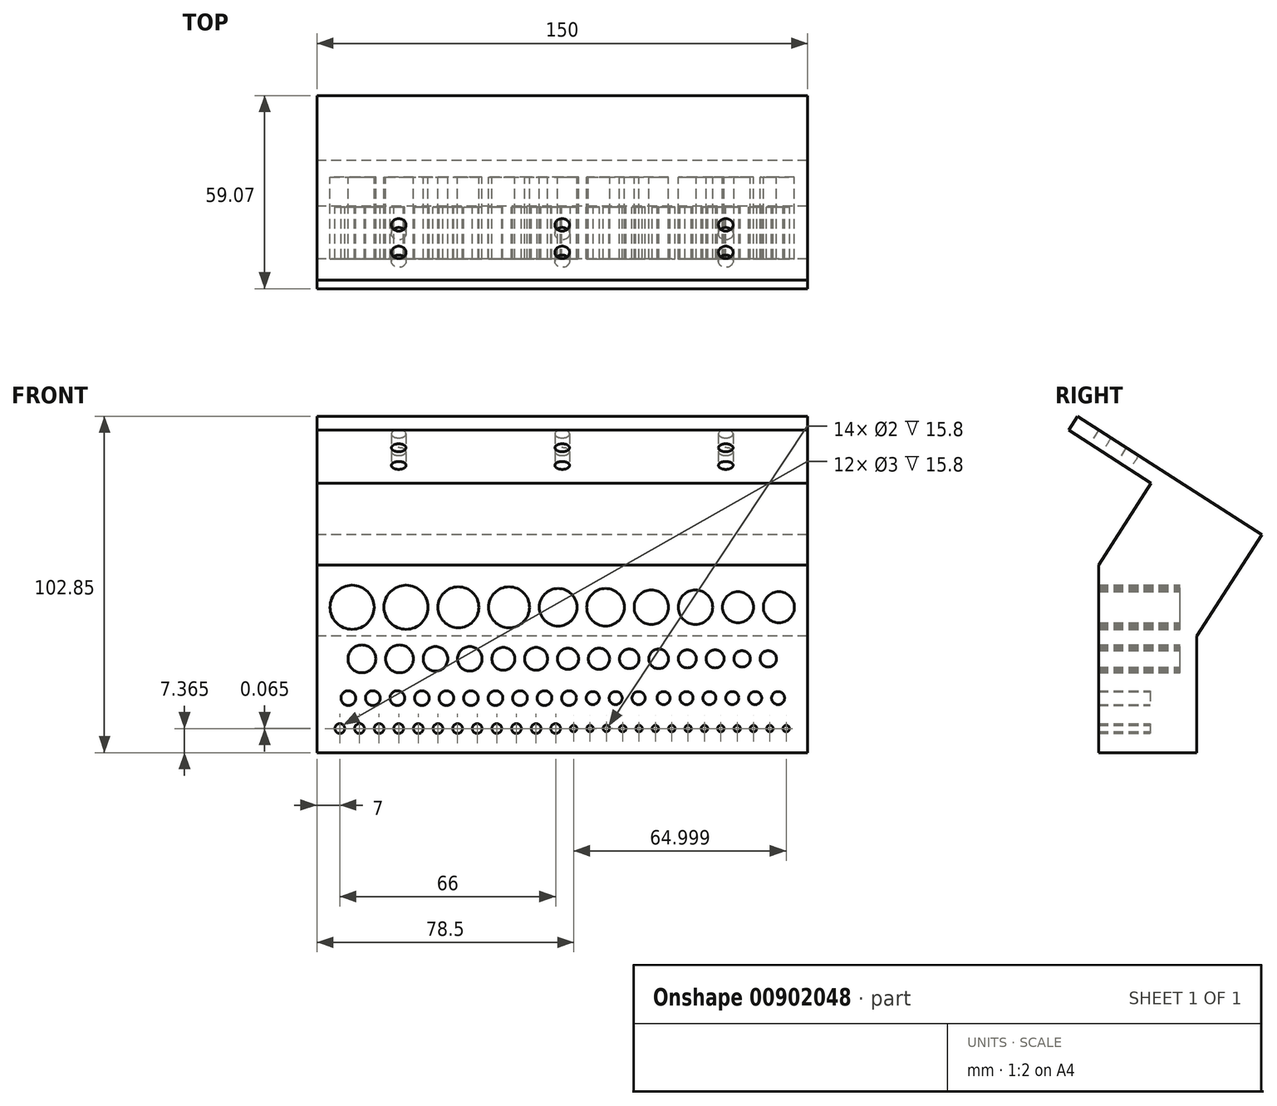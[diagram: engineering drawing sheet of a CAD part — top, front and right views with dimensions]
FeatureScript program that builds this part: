
annotation { "Feature Type Name" : "Feature", "Feature Type Description" : "" }
export const myFeature = defineFeature(function(context is Context, id is Id, definition is map)
    precondition{}
    {
        {
            var Q0;
            Q0=qCreatedBy(makeId("Front.planeOp"),FACE);
            var sketch = newSketch(context, id + "F0", { "sketchPlane" : qUnion([Q0])});
            skLineSegment(sketch, "E0.bottom", {"start": v(75, 28.68) * mm, "end": v(-75, 28.68) * mm});
            skLineSegment(sketch, "E0.top", {"start": v(75, -28.68) * mm, "end": v(-75, -28.68) * mm});
            skLineSegment(sketch, "E0.left", {"start": v(75, 28.68) * mm, "end": v(75, -28.68) * mm});
            skLineSegment(sketch, "E0.right", {"start": v(-75, 28.68) * mm, "end": v(-75, -28.68) * mm});
            skPoint(sketch, "E0.middle", {"position": v(0, 0) * mm});
            skLineSegment(sketch, "E1", {"start": v(-75, 0) * mm, "end": v(75, 0) * mm});
            skLineSegment(sketch, "E2", {"start": v(-75, 15.78) * mm, "end": v(75, 15.78) * mm});
            skLineSegment(sketch, "E3", {"start": v(-75, -12) * mm, "end": v(75, -12) * mm});
            skCircle(sketch, "E4", {"center": v(-64.25, 15.78) * mm, "radius": 6.75 * mm});
            skCircle(sketch, "E5", {"center": v(-47.75, 15.78) * mm, "radius": 6.75 * mm});
            skCircle(sketch, "E6", {"center": v(-31.75, 15.78) * mm, "radius": 6.25 * mm});
            skCircle(sketch, "E7", {"center": v(-16.25, 15.78) * mm, "radius": 6.25 * mm});
            skCircle(sketch, "E8", {"center": v(-1.25, 15.78) * mm, "radius": 5.75 * mm});
            skCircle(sketch, "E9", {"center": v(13.25, 15.78) * mm, "radius": 5.75 * mm});
            skCircle(sketch, "E10", {"center": v(27.25, 15.78) * mm, "radius": 5.25 * mm});
            skCircle(sketch, "E11", {"center": v(40.75, 15.78) * mm, "radius": 5.25 * mm});
            skCircle(sketch, "E12", {"center": v(53.75, 15.78) * mm, "radius": 4.75 * mm});
            skCircle(sketch, "E13", {"center": v(66.25, 15.78) * mm, "radius": 4.75 * mm});
            skCircle(sketch, "E14", {"center": v(-61.25, 0) * mm, "radius": 4.25 * mm});
            skCircle(sketch, "E15", {"center": v(-49.75, 0) * mm, "radius": 4.25 * mm});
            skCircle(sketch, "E16", {"center": v(-38.75, 0) * mm, "radius": 3.75 * mm});
            skCircle(sketch, "E17", {"center": v(-28.25, 0) * mm, "radius": 3.75 * mm});
            skCircle(sketch, "E18", {"center": v(-18, 0) * mm, "radius": 3.5 * mm});
            skCircle(sketch, "E19", {"center": v(-8, 0) * mm, "radius": 3.5 * mm});
            skCircle(sketch, "E20", {"center": v(1.75, 0) * mm, "radius": 3.25 * mm});
            skCircle(sketch, "E21", {"center": v(11.25, 0) * mm, "radius": 3.25 * mm});
            skCircle(sketch, "E22", {"center": v(20.5, 0) * mm, "radius": 3 * mm});
            skCircle(sketch, "E23", {"center": v(29.5, 0) * mm, "radius": 3 * mm});
            skCircle(sketch, "E24", {"center": v(38.25, 0) * mm, "radius": 2.75 * mm});
            skCircle(sketch, "E25", {"center": v(46.75, 0) * mm, "radius": 2.75 * mm});
            skCircle(sketch, "E26", {"center": v(55, 0) * mm, "radius": 2.5 * mm});
            skCircle(sketch, "E27", {"center": v(63, 0) * mm, "radius": 2.5 * mm});
            skCircle(sketch, "E28", {"center": v(-65.41, -12) * mm, "radius": 2.25 * mm});
            skCircle(sketch, "E29", {"center": v(-57.91, -12) * mm, "radius": 2.25 * mm});
            skCircle(sketch, "E30", {"center": v(-50.41, -12) * mm, "radius": 2.25 * mm});
            skCircle(sketch, "E31", {"center": v(-42.91, -12) * mm, "radius": 2.25 * mm});
            skCircle(sketch, "E32", {"center": v(-35.41, -12) * mm, "radius": 2.25 * mm});
            skCircle(sketch, "E33", {"center": v(-27.91, -12) * mm, "radius": 2.25 * mm});
            skCircle(sketch, "E34", {"center": v(-20.41, -12) * mm, "radius": 2.25 * mm});
            skCircle(sketch, "E35", {"center": v(-12.91, -12) * mm, "radius": 2.25 * mm});
            skCircle(sketch, "E36", {"center": v(-5.41, -12) * mm, "radius": 2.25 * mm});
            skCircle(sketch, "E37", {"center": v(2.09, -12) * mm, "radius": 2.25 * mm});
            skCircle(sketch, "E38", {"center": v(9.34, -12) * mm, "radius": 2 * mm});
            skCircle(sketch, "E39", {"center": v(16.34, -12) * mm, "radius": 2 * mm});
            skCircle(sketch, "E40", {"center": v(23.34, -12) * mm, "radius": 2 * mm});
            skCircle(sketch, "E41", {"center": v(31, -12) * mm, "radius": 2 * mm});
            skCircle(sketch, "E42", {"center": v(38, -12) * mm, "radius": 2 * mm});
            skCircle(sketch, "E43", {"center": v(45, -12) * mm, "radius": 2 * mm});
            skCircle(sketch, "E44", {"center": v(52, -12) * mm, "radius": 2 * mm});
            skCircle(sketch, "E45", {"center": v(59, -12) * mm, "radius": 2 * mm});
            skCircle(sketch, "E46", {"center": v(66, -12) * mm, "radius": 2 * mm});
            skLineSegment(sketch, "E47", {"start": v(-75, -21.32) * mm, "end": v(75, -21.32) * mm});
            skCircle(sketch, "E48", {"center": v(-68, -21.32) * mm, "radius": 1.5 * mm});
            skCircle(sketch, "E49", {"center": v(-62, -21.32) * mm, "radius": 1.5 * mm});
            skCircle(sketch, "E50", {"center": v(-56, -21.32) * mm, "radius": 1.5 * mm});
            skCircle(sketch, "E51", {"center": v(-50, -21.32) * mm, "radius": 1.5 * mm});
            skCircle(sketch, "E52", {"center": v(-44, -21.32) * mm, "radius": 1.5 * mm});
            skCircle(sketch, "E53", {"center": v(-38, -21.32) * mm, "radius": 1.5 * mm});
            skCircle(sketch, "E54", {"center": v(-32, -21.32) * mm, "radius": 1.5 * mm});
            skCircle(sketch, "E55", {"center": v(-26, -21.32) * mm, "radius": 1.5 * mm});
            skCircle(sketch, "E56", {"center": v(-20, -21.32) * mm, "radius": 1.5 * mm});
            skCircle(sketch, "E57", {"center": v(-14, -21.32) * mm, "radius": 1.5 * mm});
            skCircle(sketch, "E58", {"center": v(-8, -21.32) * mm, "radius": 1.5 * mm});
            skCircle(sketch, "E59", {"center": v(-2, -21.32) * mm, "radius": 1.5 * mm});
            skCircle(sketch, "E60", {"center": v(3.5, -21.32) * mm, "radius": 1 * mm});
            skCircle(sketch, "E61", {"center": v(8.5, -21.32) * mm, "radius": 1 * mm});
            skCircle(sketch, "E62", {"center": v(13.5, -21.25) * mm, "radius": 1 * mm});
            skCircle(sketch, "E63", {"center": v(18.5, -21.32) * mm, "radius": 1 * mm});
            skCircle(sketch, "E64", {"center": v(23.5, -21.32) * mm, "radius": 1 * mm});
            skCircle(sketch, "E65", {"center": v(28.5, -21.32) * mm, "radius": 1 * mm});
            skCircle(sketch, "E66", {"center": v(33.5, -21.32) * mm, "radius": 1 * mm});
            skCircle(sketch, "E67", {"center": v(38.5, -21.32) * mm, "radius": 1 * mm});
            skCircle(sketch, "E68", {"center": v(43.5, -21.32) * mm, "radius": 1 * mm});
            skCircle(sketch, "E69", {"center": v(48.5, -21.32) * mm, "radius": 1 * mm});
            skCircle(sketch, "E70", {"center": v(53.5, -21.32) * mm, "radius": 1 * mm});
            skCircle(sketch, "E71", {"center": v(58.5, -21.32) * mm, "radius": 1 * mm});
            skCircle(sketch, "E72", {"center": v(63.5, -21.32) * mm, "radius": 1 * mm});
            skCircle(sketch, "E73", {"center": v(68.5, -21.32) * mm, "radius": 1 * mm});
            skSolve(sketch);
        }
        {
            var Q0;
            Q0 = qSketchRegion(id + "F0", true);
            extrude(context, id + "F1", {"entities" : qUnion([Q0]), "depth" : 25 * mm, "offsetDistance" : 25 * mm});
        }
        {
            var Q0;
            Q0=makeQuery(id+"F1.opExtrude","CAP_FACE",FACE,{"disambiguationData":[OSD([sQuery(id+"F0.wireOp",EDGE,"E0.bottom"),sQuery(id+"F0.wireOp",EDGE,"E0.top"),sQuery(id+"F0.wireOp",EDGE,"E0.left"),sQuery(id+"F0.wireOp",EDGE,"E0.right"),sQuery(id+"F0.wireOp",EDGE,"E4"),sQuery(id+"F0.wireOp",EDGE,"E5"),sQuery(id+"F0.wireOp",EDGE,"E6"),sQuery(id+"F0.wireOp",EDGE,"E7"),sQuery(id+"F0.wireOp",EDGE,"E8"),sQuery(id+"F0.wireOp",EDGE,"E9"),sQuery(id+"F0.wireOp",EDGE,"E10"),sQuery(id+"F0.wireOp",EDGE,"E11"),sQuery(id+"F0.wireOp",EDGE,"E12"),sQuery(id+"F0.wireOp",EDGE,"E13"),sQuery(id+"F0.wireOp",EDGE,"E14"),sQuery(id+"F0.wireOp",EDGE,"E15"),sQuery(id+"F0.wireOp",EDGE,"E16"),sQuery(id+"F0.wireOp",EDGE,"E17"),sQuery(id+"F0.wireOp",EDGE,"E18"),sQuery(id+"F0.wireOp",EDGE,"E19"),sQuery(id+"F0.wireOp",EDGE,"E20"),sQuery(id+"F0.wireOp",EDGE,"E21"),sQuery(id+"F0.wireOp",EDGE,"E22"),sQuery(id+"F0.wireOp",EDGE,"E23"),sQuery(id+"F0.wireOp",EDGE,"E24"),sQuery(id+"F0.wireOp",EDGE,"E25"),sQuery(id+"F0.wireOp",EDGE,"E26"),sQuery(id+"F0.wireOp",EDGE,"E27"),sQuery(id+"F0.wireOp",EDGE,"E28"),sQuery(id+"F0.wireOp",EDGE,"E29"),sQuery(id+"F0.wireOp",EDGE,"E30"),sQuery(id+"F0.wireOp",EDGE,"E31"),sQuery(id+"F0.wireOp",EDGE,"E32"),sQuery(id+"F0.wireOp",EDGE,"E33"),sQuery(id+"F0.wireOp",EDGE,"E34"),sQuery(id+"F0.wireOp",EDGE,"E35"),sQuery(id+"F0.wireOp",EDGE,"E36"),sQuery(id+"F0.wireOp",EDGE,"E37"),sQuery(id+"F0.wireOp",EDGE,"E38"),sQuery(id+"F0.wireOp",EDGE,"E39"),sQuery(id+"F0.wireOp",EDGE,"E40"),sQuery(id+"F0.wireOp",EDGE,"E41"),sQuery(id+"F0.wireOp",EDGE,"E42"),sQuery(id+"F0.wireOp",EDGE,"E43"),sQuery(id+"F0.wireOp",EDGE,"E44"),sQuery(id+"F0.wireOp",EDGE,"E45"),sQuery(id+"F0.wireOp",EDGE,"E46"),sQuery(id+"F0.wireOp",EDGE,"E48"),sQuery(id+"F0.wireOp",EDGE,"E49"),sQuery(id+"F0.wireOp",EDGE,"E50"),sQuery(id+"F0.wireOp",EDGE,"E51"),sQuery(id+"F0.wireOp",EDGE,"E52"),sQuery(id+"F0.wireOp",EDGE,"E53"),sQuery(id+"F0.wireOp",EDGE,"E54"),sQuery(id+"F0.wireOp",EDGE,"E55"),sQuery(id+"F0.wireOp",EDGE,"E56"),sQuery(id+"F0.wireOp",EDGE,"E57"),sQuery(id+"F0.wireOp",EDGE,"E58"),sQuery(id+"F0.wireOp",EDGE,"E59"),sQuery(id+"F0.wireOp",EDGE,"E60"),sQuery(id+"F0.wireOp",EDGE,"E61"),sQuery(id+"F0.wireOp",EDGE,"E62"),sQuery(id+"F0.wireOp",EDGE,"E63"),sQuery(id+"F0.wireOp",EDGE,"E64"),sQuery(id+"F0.wireOp",EDGE,"E65"),sQuery(id+"F0.wireOp",EDGE,"E66"),sQuery(id+"F0.wireOp",EDGE,"E67"),sQuery(id+"F0.wireOp",EDGE,"E68"),sQuery(id+"F0.wireOp",EDGE,"E69"),sQuery(id+"F0.wireOp",EDGE,"E70"),sQuery(id+"F0.wireOp",EDGE,"E71"),sQuery(id+"F0.wireOp",EDGE,"E72"),sQuery(id+"F0.wireOp",EDGE,"E73")])],"isStart":true});
            var sketch = newSketch(context, id + "F2", { "sketchPlane" : qUnion([Q0])});
            skLineSegment(sketch, "E74.bottom", {"start": v(-72.47, -7.03) * mm, "end": v(72.05, -7.03) * mm});
            skLineSegment(sketch, "E74.top", {"start": v(-72.47, -24.86) * mm, "end": v(72.05, -24.86) * mm});
            skLineSegment(sketch, "E74.left", {"start": v(-72.47, -7.03) * mm, "end": v(-72.47, -24.86) * mm});
            skLineSegment(sketch, "E74.right", {"start": v(72.05, -7.03) * mm, "end": v(72.05, -24.86) * mm});
            skSolve(sketch);
        }
        {
            var Q0;
            Q0 = qSketchRegion(id + "F2", true);
            extrude(context, id + "F3", {"entities" : qUnion([Q0]), "operationType" : NewBodyOperationType.ADD, "oppositeDirection" : true, "depth" : 9.2 * mm, "offsetDistance" : 25 * mm});
        }
        {
            var Q0;
            Q0=makeQuery(id+"F3.boolean.opBoolean","MERGE",FACE,{"derivedFrom":[makeQuery(id+"F1.opExtrude","CAP_FACE",FACE,{"disambiguationData":[OSD([sQuery(id+"F0.wireOp",EDGE,"E0.bottom"),sQuery(id+"F0.wireOp",EDGE,"E0.top"),sQuery(id+"F0.wireOp",EDGE,"E0.left"),sQuery(id+"F0.wireOp",EDGE,"E0.right"),sQuery(id+"F0.wireOp",EDGE,"E4"),sQuery(id+"F0.wireOp",EDGE,"E5"),sQuery(id+"F0.wireOp",EDGE,"E6"),sQuery(id+"F0.wireOp",EDGE,"E7"),sQuery(id+"F0.wireOp",EDGE,"E8"),sQuery(id+"F0.wireOp",EDGE,"E9"),sQuery(id+"F0.wireOp",EDGE,"E10"),sQuery(id+"F0.wireOp",EDGE,"E11"),sQuery(id+"F0.wireOp",EDGE,"E12"),sQuery(id+"F0.wireOp",EDGE,"E13"),sQuery(id+"F0.wireOp",EDGE,"E14"),sQuery(id+"F0.wireOp",EDGE,"E15"),sQuery(id+"F0.wireOp",EDGE,"E16"),sQuery(id+"F0.wireOp",EDGE,"E17"),sQuery(id+"F0.wireOp",EDGE,"E18"),sQuery(id+"F0.wireOp",EDGE,"E19"),sQuery(id+"F0.wireOp",EDGE,"E20"),sQuery(id+"F0.wireOp",EDGE,"E21"),sQuery(id+"F0.wireOp",EDGE,"E22"),sQuery(id+"F0.wireOp",EDGE,"E23"),sQuery(id+"F0.wireOp",EDGE,"E24"),sQuery(id+"F0.wireOp",EDGE,"E25"),sQuery(id+"F0.wireOp",EDGE,"E26"),sQuery(id+"F0.wireOp",EDGE,"E27"),sQuery(id+"F0.wireOp",EDGE,"E28"),sQuery(id+"F0.wireOp",EDGE,"E29"),sQuery(id+"F0.wireOp",EDGE,"E30"),sQuery(id+"F0.wireOp",EDGE,"E31"),sQuery(id+"F0.wireOp",EDGE,"E32"),sQuery(id+"F0.wireOp",EDGE,"E33"),sQuery(id+"F0.wireOp",EDGE,"E34"),sQuery(id+"F0.wireOp",EDGE,"E35"),sQuery(id+"F0.wireOp",EDGE,"E36"),sQuery(id+"F0.wireOp",EDGE,"E37"),sQuery(id+"F0.wireOp",EDGE,"E38"),sQuery(id+"F0.wireOp",EDGE,"E39"),sQuery(id+"F0.wireOp",EDGE,"E40"),sQuery(id+"F0.wireOp",EDGE,"E41"),sQuery(id+"F0.wireOp",EDGE,"E42"),sQuery(id+"F0.wireOp",EDGE,"E43"),sQuery(id+"F0.wireOp",EDGE,"E44"),sQuery(id+"F0.wireOp",EDGE,"E45"),sQuery(id+"F0.wireOp",EDGE,"E46"),sQuery(id+"F0.wireOp",EDGE,"E48"),sQuery(id+"F0.wireOp",EDGE,"E49"),sQuery(id+"F0.wireOp",EDGE,"E50"),sQuery(id+"F0.wireOp",EDGE,"E51"),sQuery(id+"F0.wireOp",EDGE,"E52"),sQuery(id+"F0.wireOp",EDGE,"E53"),sQuery(id+"F0.wireOp",EDGE,"E54"),sQuery(id+"F0.wireOp",EDGE,"E55"),sQuery(id+"F0.wireOp",EDGE,"E56"),sQuery(id+"F0.wireOp",EDGE,"E57"),sQuery(id+"F0.wireOp",EDGE,"E58"),sQuery(id+"F0.wireOp",EDGE,"E59"),sQuery(id+"F0.wireOp",EDGE,"E60"),sQuery(id+"F0.wireOp",EDGE,"E61"),sQuery(id+"F0.wireOp",EDGE,"E62"),sQuery(id+"F0.wireOp",EDGE,"E63"),sQuery(id+"F0.wireOp",EDGE,"E64"),sQuery(id+"F0.wireOp",EDGE,"E65"),sQuery(id+"F0.wireOp",EDGE,"E66"),sQuery(id+"F0.wireOp",EDGE,"E67"),sQuery(id+"F0.wireOp",EDGE,"E68"),sQuery(id+"F0.wireOp",EDGE,"E69"),sQuery(id+"F0.wireOp",EDGE,"E70"),sQuery(id+"F0.wireOp",EDGE,"E71"),sQuery(id+"F0.wireOp",EDGE,"E72"),sQuery(id+"F0.wireOp",EDGE,"E73")])],"isStart":true}),makeQuery(id+"F3.opExtrude","CAP_FACE",FACE,{"disambiguationData":[OSD([sQuery(id+"F2.wireOp",EDGE,"E74.bottom"),sQuery(id+"F2.wireOp",EDGE,"E74.top"),sQuery(id+"F2.wireOp",EDGE,"E74.left"),sQuery(id+"F2.wireOp",EDGE,"E74.right")])],"isStart":true})]});
            var sketch = newSketch(context, id + "F4", { "sketchPlane" : qUnion([Q0])});
            skLineSegment(sketch, "E75.bottom", {"start": v(-75, 28.68) * mm, "end": v(75, 28.68) * mm});
            skLineSegment(sketch, "E75.top", {"start": v(-75, -28.68) * mm, "end": v(75, -28.68) * mm});
            skLineSegment(sketch, "E75.left", {"start": v(-75, 28.68) * mm, "end": v(-75, -28.68) * mm});
            skLineSegment(sketch, "E75.right", {"start": v(75, 28.68) * mm, "end": v(75, -28.68) * mm});
            skSolve(sketch);
        }
        {
            var Q0;
            Q0 = qSketchRegion(id + "F4", true);
            extrude(context, id + "F5", {"entities" : qUnion([Q0]), "operationType" : NewBodyOperationType.ADD, "depth" : 5 * mm, "offsetDistance" : 25 * mm});
        }
        {
            var Q0;
            Q0=makeQuery(id+"F5.boolean.opBoolean","MERGE",FACE,{"derivedFrom":[makeQuery(id+"F1.opExtrude","SWEPT_FACE",FACE,{"disambiguationData":[OSD([sQuery(id+"F0.wireOp",EDGE,"E0.right")])]}),makeQuery(id+"F5.opExtrude","SWEPT_FACE",FACE,{"disambiguationData":[OSD([sQuery(id+"F4.wireOp",EDGE,"E75.right")])]})]});
            var sketch = newSketch(context, id + "F6", { "sketchPlane" : qUnion([Q0])});
            skLineSegment(sketch, "E76", {"start": v(-5, 6.95) * mm, "end": v(-24.92, 37.99) * mm});
            skLineSegment(sketch, "E77", {"start": v(-24.92, 37.99) * mm, "end": v(31.45, 74.17) * mm});
            skLineSegment(sketch, "E78", {"start": v(31.45, 74.17) * mm, "end": v(34.15, 69.96) * mm});
            skLineSegment(sketch, "E79", {"start": v(34.15, 69.96) * mm, "end": v(8.9, 53.76) * mm});
            skLineSegment(sketch, "E80", {"start": v(8.9, 53.76) * mm, "end": v(25, 28.68) * mm});
            skLineSegment(sketch, "E81", {"start": v(25, 28.68) * mm, "end": v(-3.26, 27.63) * mm});
            skLineSegment(sketch, "E82", {"start": v(-3.26, 27.63) * mm, "end": v(-5, 6.95) * mm});
            skSolve(sketch);
        }
        {
            var Q0;
            Q0 = qSketchRegion(id + "F6", true);
            extrude(context, id + "F7", {"entities" : qUnion([Q0]), "operationType" : NewBodyOperationType.ADD, "oppositeDirection" : true, "depth" : 150 * mm, "offsetDistance" : 25 * mm});
        }
        {
            var Q0;
            Q0=makeQuery(id+"F7.opExtrude","SWEPT_FACE",FACE,{"disambiguationData":[OSD([sQuery(id+"F6.wireOp",EDGE,"E79")])]});
            var sketch = newSketch(context, id + "F8", { "sketchPlane" : qUnion([Q0])});
            skLineSegment(sketch, "E83", {"start": v(-75, 56.53) * mm, "end": v(75, 56.53) * mm});
            skLineSegment(sketch, "E84", {"start": v(75, 46.53) * mm, "end": v(-75, 46.53) * mm});
            skCircle(sketch, "E85", {"center": v(-50, 56.53) * mm, "radius": 2.25 * mm});
            skCircle(sketch, "E86", {"center": v(0, 56.53) * mm, "radius": 2.25 * mm});
            skCircle(sketch, "E87", {"center": v(50, 56.53) * mm, "radius": 2.25 * mm});
            skCircle(sketch, "E88", {"center": v(-50, 46.53) * mm, "radius": 2.25 * mm});
            skCircle(sketch, "E89", {"center": v(0, 46.53) * mm, "radius": 2.25 * mm});
            skCircle(sketch, "E90", {"center": v(50, 46.53) * mm, "radius": 2.25 * mm});
            skSolve(sketch);
        }
        {
            var Q0;
            Q0 = qSketchRegion(id + "F8", true);
            extrude(context, id + "F9", {"entities" : qUnion([Q0]), "operationType" : NewBodyOperationType.REMOVE, "oppositeDirection" : true, "depth" : 25 * mm, "offsetDistance" : 25 * mm});
        }
    });
